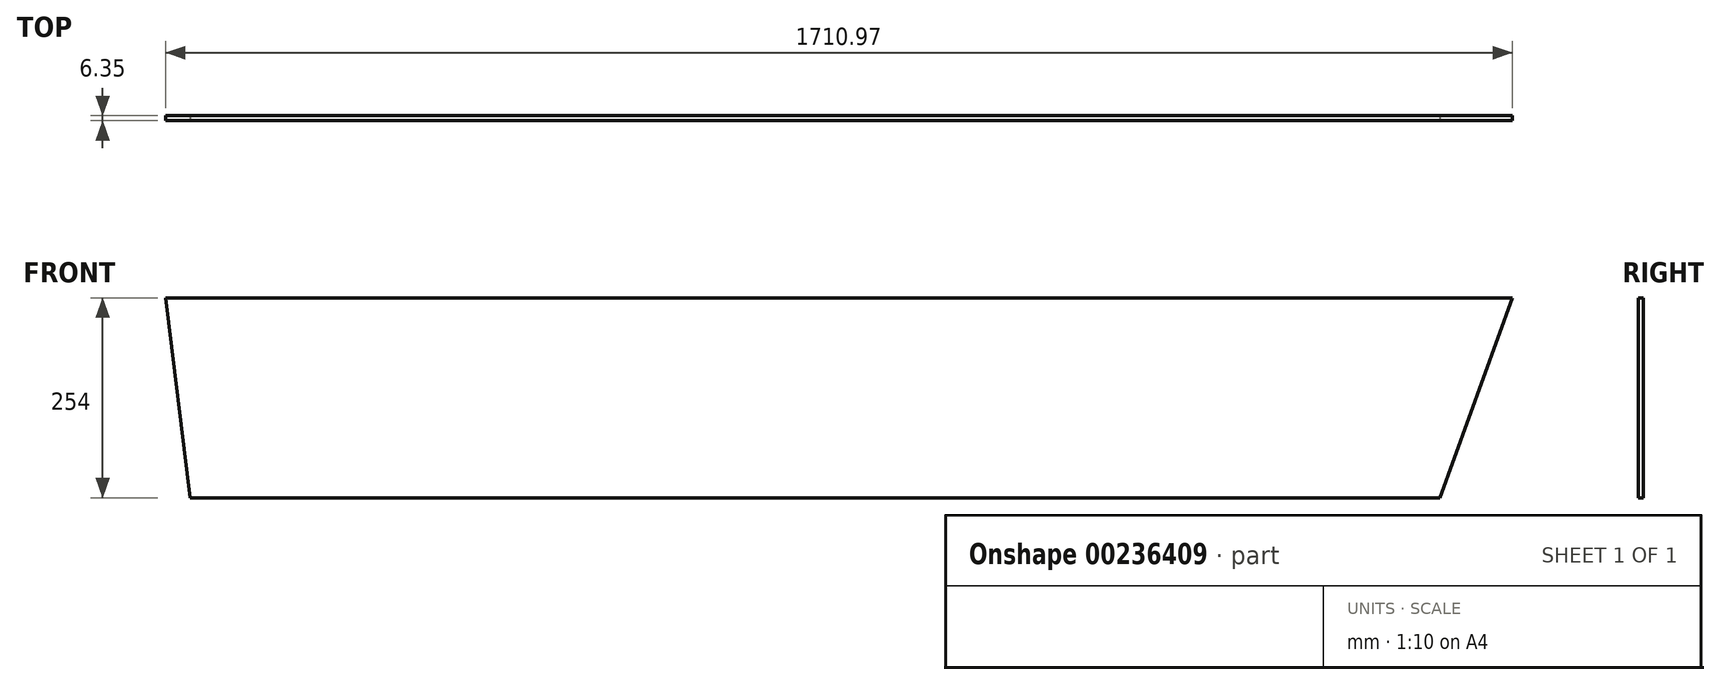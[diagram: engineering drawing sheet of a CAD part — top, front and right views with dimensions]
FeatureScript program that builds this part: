
annotation { "Feature Type Name" : "Feature", "Feature Type Description" : "" }
export const myFeature = defineFeature(function(context is Context, id is Id, definition is map)
    precondition{}
    {
        {
            var Q0;
            Q0=qCreatedBy(makeId("Front.planeOp"),FACE);
            var sketch = newSketch(context, id + "F0", { "sketchPlane" : qUnion([Q0])});
            skLineSegment(sketch, "E0", {"start": v(-808.75, -127) * mm, "end": v(-840.25, 127) * mm});
            skLineSegment(sketch, "E1", {"start": v(-840.25, 127) * mm, "end": v(870.72, 127) * mm});
            skLineSegment(sketch, "E2", {"start": v(870.72, 127) * mm, "end": v(778.27, -127) * mm});
            skLineSegment(sketch, "E3", {"start": v(778.27, -127) * mm, "end": v(-808.75, -127) * mm});
            skSolve(sketch);
        }
        {
            var Q0;
            Q0 = qSketchRegion(id + "F0", true);
            extrude(context, id + "F1", {"entities" : qUnion([Q0]), "oppositeDirection" : true, "depth" : 6.35 * mm});
        }
    });
